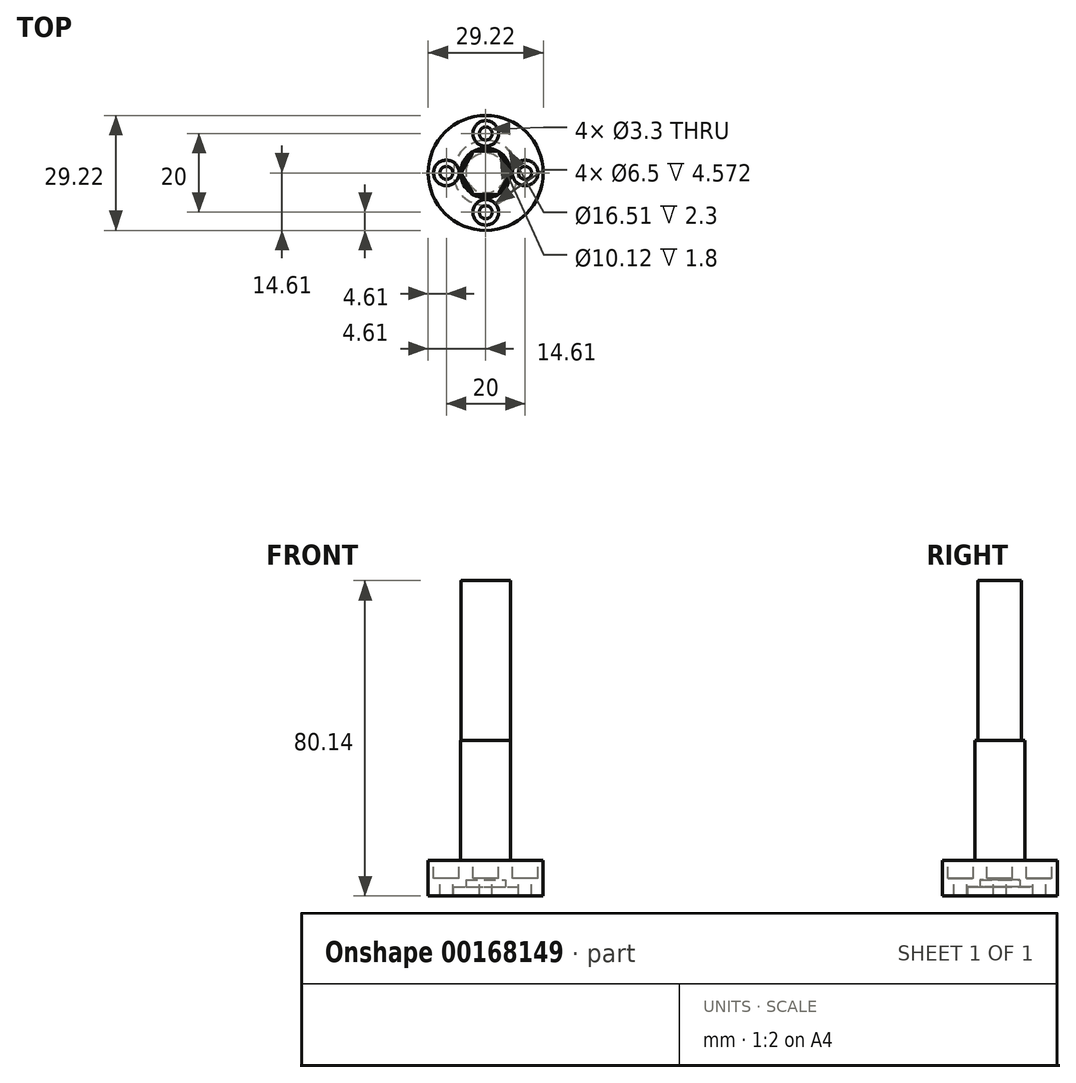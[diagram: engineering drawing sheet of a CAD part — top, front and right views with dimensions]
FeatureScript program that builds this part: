
annotation { "Feature Type Name" : "Feature", "Feature Type Description" : "" }
export const myFeature = defineFeature(function(context is Context, id is Id, definition is map)
    precondition{}
    {
        {
            var Q0;
            Q0=qCreatedBy(makeId("Top.planeOp"),FACE);
            var sketch = newSketch(context, id + "F0", { "sketchPlane" : qUnion([Q0])});
            skCircle(sketch, "E0", {"center": v(0, 0) * mm, "radius": 14.6 * mm});
            skSolve(sketch);
        }
        {
            var Q0;
            Q0=makeQuery(id+"F0.imprint","IMPRINT",FACE,{"disambiguationData":[TD([[makeQuery(id+"F0.imprint","IMPRINT",EDGE,{"derivedFrom":sQuery(id+"F0.wireOp",EDGE,"E0")}),1.0]])]});
            extrude(context, id + "F1", {"entities" : qUnion([Q0]), "depth" : 9.02 * mm});
        }
        {
            var Q0;
            Q0=makeQuery(id+"F1.opExtrude","CAP_FACE",FACE,{"disambiguationData":[OSD([sQuery(id+"F0.wireOp",EDGE,"E0")])],"isStart":false});
            var sketch = newSketch(context, id + "F2", { "sketchPlane" : qUnion([Q0])});
            skCircle(sketch, "E1", {"center": v(0, 0) * mm, "radius": 6.35 * mm});
            skSolve(sketch);
        }
        {
            var Q0;
            Q0=qSketchRegion(id+"F2",true);
            extrude(context, id + "F3", {"entities" : qUnion([Q0]), "operationType" : NewBodyOperationType.ADD, "depth" : 30.48 * mm});
        }
        {
            var Q0;
            Q0=makeQuery(id+"F3.opExtrude","CAP_FACE",FACE,{"disambiguationData":[OSD([sQuery(id+"F2.wireOp",EDGE,"E1")])],"isStart":false});
            var sketch = newSketch(context, id + "F4", { "sketchPlane" : qUnion([Q0])});
            skCircle(sketch, "E2.cCircle", {"center": v(0, 0) * mm, "radius": 5.54 * mm, "construction": true});
            skLineSegment(sketch, "E2.0", {"start": v(6.17, -0.38) * mm, "end": v(3.42, -5.16) * mm});
            skLineSegment(sketch, "E2.1", {"start": v(2.76, -5.54) * mm, "end": v(-2.76, -5.54) * mm});
            skLineSegment(sketch, "E2.2", {"start": v(-3.42, -5.16) * mm, "end": v(-6.17, -0.38) * mm});
            skLineSegment(sketch, "E2.3", {"start": v(-6.17, 0.38) * mm, "end": v(-3.42, 5.16) * mm});
            skLineSegment(sketch, "E2.4", {"start": v(-2.76, 5.54) * mm, "end": v(2.76, 5.54) * mm});
            skLineSegment(sketch, "E2.5", {"start": v(3.42, 5.16) * mm, "end": v(6.17, 0.38) * mm});
            skPoint(sketch, "E2.0.midPoint", {"position": v(4.8, -2.77) * mm});
            skPoint(sketch, "E3.visualSharp", {"position": v(-3.2, 5.54) * mm});
            skArc(sketch, "E3.filletArc", {"start": v(-2.76, 5.54) * mm, "mid": v(-3.14, 5.44) * mm, "end": v(-3.42, 5.16) * mm});
            skPoint(sketch, "E4.visualSharp", {"position": v(3.2, 5.54) * mm});
            skArc(sketch, "E4.filletArc", {"start": v(3.42, 5.16) * mm, "mid": v(3.14, 5.44) * mm, "end": v(2.76, 5.54) * mm});
            skPoint(sketch, "E5.visualSharp", {"position": v(6.4, 0) * mm});
            skArc(sketch, "E5.filletArc", {"start": v(6.17, -0.38) * mm, "mid": v(6.28, 0) * mm, "end": v(6.17, 0.38) * mm});
            skPoint(sketch, "E6.visualSharp", {"position": v(3.2, -5.54) * mm});
            skArc(sketch, "E6.filletArc", {"start": v(2.76, -5.54) * mm, "mid": v(3.14, -5.44) * mm, "end": v(3.42, -5.16) * mm});
            skPoint(sketch, "E7.visualSharp", {"position": v(-3.2, -5.54) * mm});
            skArc(sketch, "E7.filletArc", {"start": v(-3.42, -5.16) * mm, "mid": v(-3.14, -5.44) * mm, "end": v(-2.76, -5.54) * mm});
            skPoint(sketch, "E8.visualSharp", {"position": v(-6.4, 0) * mm});
            skArc(sketch, "E8.filletArc", {"start": v(-6.17, 0.38) * mm, "mid": v(-6.28, 0) * mm, "end": v(-6.17, -0.38) * mm});
            skSolve(sketch);
        }
        {
            var Q0;
            Q0=makeQuery(id+"F4.imprint","IMPRINT",FACE,{"disambiguationData":[TD([[makeQuery(id+"F4.imprint","IMPRINT",EDGE,{"derivedFrom":sQuery(id+"F4.wireOp",EDGE,"E2.0")}),-1.0]])]});
            extrude(context, id + "F5", {"entities" : qUnion([Q0]), "operationType" : NewBodyOperationType.ADD, "depth" : 40.64 * mm});
        }
        {
            var Q0;
            Q0=makeQuery(id+"F1.opExtrude","CAP_FACE",FACE,{"disambiguationData":[OSD([sQuery(id+"F0.wireOp",EDGE,"E0")])],"isStart":true});
            var sketch = newSketch(context, id + "F6", { "sketchPlane" : qUnion([Q0])});
            skCircle(sketch, "E9", {"center": v(0, 0) * mm, "radius": 8.26 * mm});
            skSolve(sketch);
        }
        {
            var Q0;
            Q0=qSketchRegion(id+"F6",true);
            extrude(context, id + "F7", {"entities" : qUnion([Q0]), "operationType" : NewBodyOperationType.REMOVE, "oppositeDirection" : true, "depth" : 2.3 * mm});
        }
        {
            var Q0;
            Q0=makeQuery(id+"F1.opExtrude","CAP_FACE",FACE,{"disambiguationData":[OSD([sQuery(id+"F0.wireOp",EDGE,"E0")])],"isStart":true});
            var sketch = newSketch(context, id + "F8", { "sketchPlane" : qUnion([Q0])});
            skCircle(sketch, "E10", {"center": v(0, 0) * mm, "radius": 5.06 * mm});
            skSolve(sketch);
        }
        {
            var Q0;
            Q0=qSketchRegion(id+"F8",true);
            extrude(context, id + "F9", {"entities" : qUnion([Q0]), "operationType" : NewBodyOperationType.REMOVE, "oppositeDirection" : true, "depth" : 4.1 * mm});
        }
        {
            var Q0;
            Q0=makeQuery(id+"F1.opExtrude","CAP_FACE",FACE,{"disambiguationData":[OSD([sQuery(id+"F0.wireOp",EDGE,"E0")])],"isStart":false});
            var sketch = newSketch(context, id + "F10", { "sketchPlane" : qUnion([Q0])});
            skPoint(sketch, "E11", {"position": v(-10, 0) * mm});
            skPoint(sketch, "E12", {"position": v(0, 10) * mm});
            skPoint(sketch, "E13", {"position": v(10, 0) * mm});
            skPoint(sketch, "E14", {"position": v(0, -10) * mm});
            skCircle(sketch, "E15", {"center": v(0, 0) * mm, "radius": 10 * mm, "construction": true});
            skSolve(sketch);
        }
        {
            var Q0;
            Q0=sQuery(id+"F10.wireOp",VERTEX,"E14");
            var Q1;
            Q1=sQuery(id+"F10.wireOp",VERTEX,"E11");
            var Q2;
            Q2=sQuery(id+"F10.wireOp",VERTEX,"E12");
            var Q3;
            Q3=sQuery(id+"F10.wireOp",VERTEX,"E13");
            var Q4;
            Q4=makeQuery(id+"F1.opExtrude","SWEPT_BODY",BODY,{"disambiguationData":[OSD([sQuery(id+"F0.wireOp",EDGE,"E0")])]});
            hole(context, id + "F11", {"style" : HoleStyle.C_BORE, "endStyle" : HoleEndStyle.THROUGH, "holeDiameter" : 3.3 * mm, "cBoreDiameter" : 6.5 * mm, "cBoreDepth" : 4.57 * mm, "locations" : qUnion([Q0, Q1, Q2, Q3]), "scope" : qUnion([Q4]), "isTappedThrough" : true});
        }
    });
